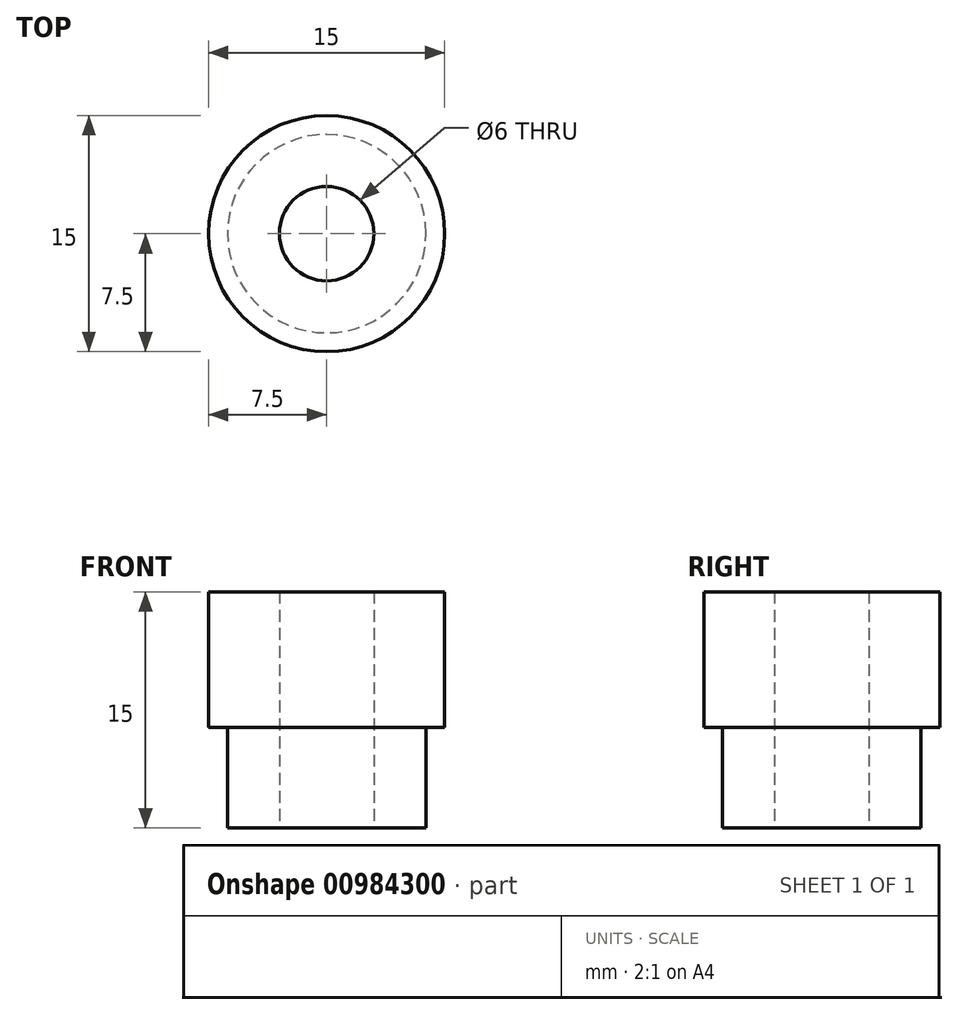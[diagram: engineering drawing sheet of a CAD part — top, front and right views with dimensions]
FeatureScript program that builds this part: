
annotation { "Feature Type Name" : "Feature", "Feature Type Description" : "" }
export const myFeature = defineFeature(function(context is Context, id is Id, definition is map)
    precondition{}
    {
        {
            var Q0;
            Q0=qCreatedBy(makeId("Top.planeOp"),FACE);
            var sketch = newSketch(context, id + "F0", { "sketchPlane" : qUnion([Q0])});
            skCircle(sketch, "E0", {"center": v(0, 0) * mm, "radius": 7.5 * mm});
            skCircle(sketch, "E1", {"center": v(0, 0) * mm, "radius": 3 * mm});
            skSolve(sketch);
        }
        {
            var Q0;
            Q0 = qSketchRegion(id + "F0", true);
            extrude(context, id + "F1", {"entities" : qUnion([Q0]), "depth" : 15 * mm, "offsetDistance" : 25 * mm});
        }
        {
            var Q0;
            Q0=qCreatedBy(makeId("Top.planeOp"),FACE);
            var sketch = newSketch(context, id + "F2", { "sketchPlane" : qUnion([Q0])});
            skCircle(sketch, "E2", {"center": v(0, 0) * mm, "radius": 6.3 * mm});
            skCircle(sketch, "E3.0", {"center": v(0, 0) * mm, "radius": 7.5 * mm});
            skSolve(sketch);
        }
        {
            var Q0;
            Q0 = qSketchRegion(id + "F2", true);
            extrude(context, id + "F3", {"entities" : qUnion([Q0]), "operationType" : NewBodyOperationType.REMOVE, "depth" : (12.8 / 2) * mm, "offsetDistance" : 25 * mm});
        }
    });
